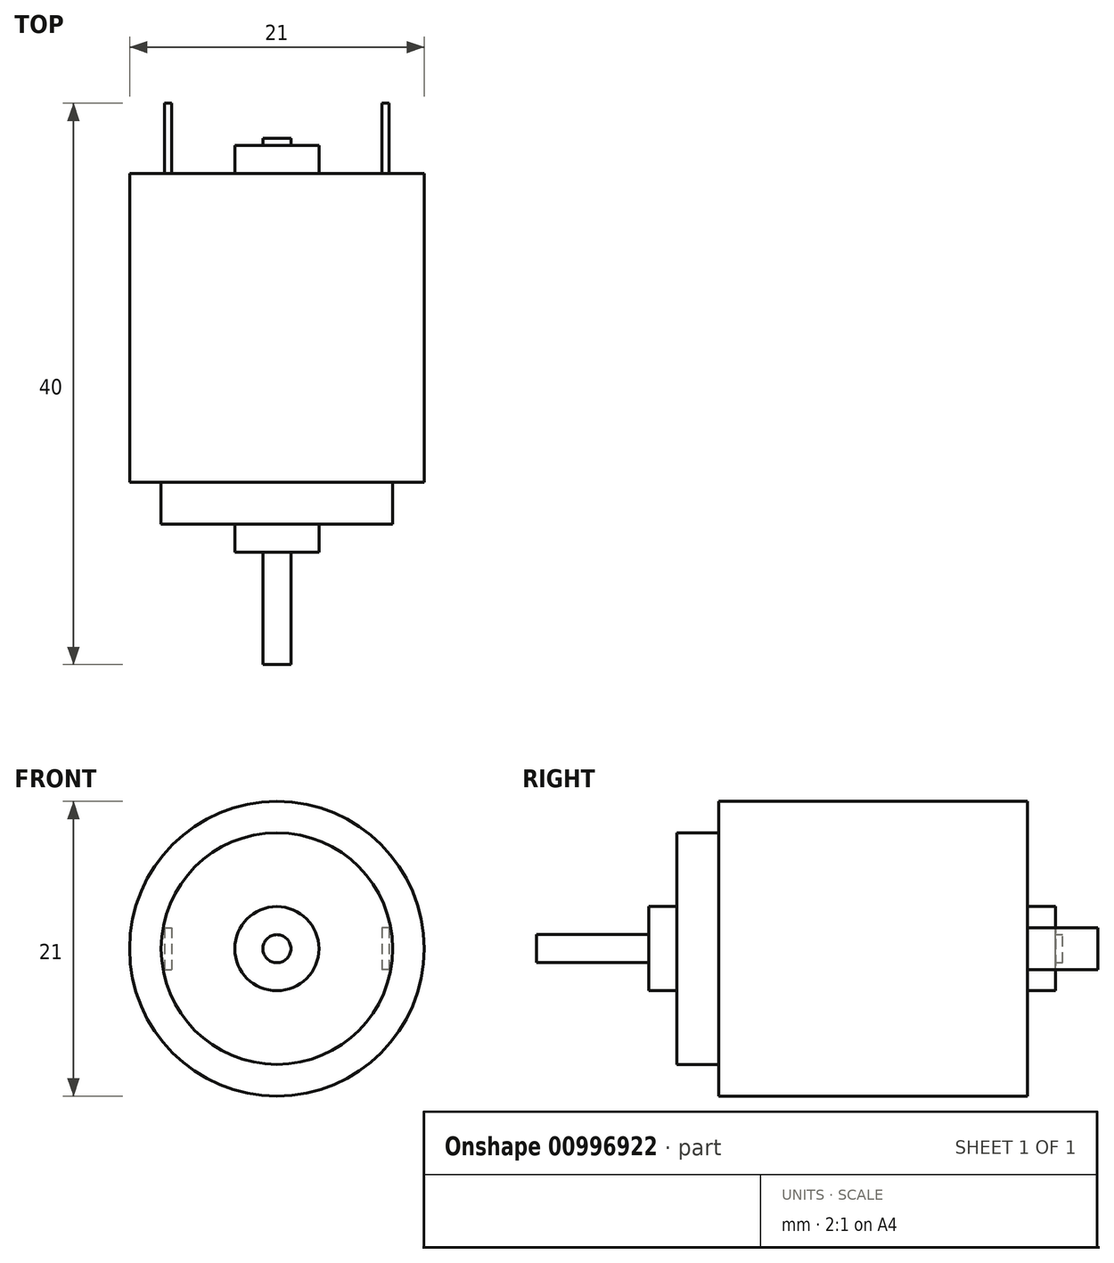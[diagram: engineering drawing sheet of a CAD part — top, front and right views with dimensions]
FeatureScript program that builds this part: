
annotation { "Feature Type Name" : "Feature", "Feature Type Description" : "" }
export const myFeature = defineFeature(function(context is Context, id is Id, definition is map)
    precondition{}
    {
        {
            var Q0;
            Q0=qCreatedBy(makeId("Front.planeOp"),FACE);
            var sketch = newSketch(context, id + "F0", { "sketchPlane" : qUnion([Q0])});
            skCircle(sketch, "E0", {"center": v(0, 0) * mm, "radius": 10.5 * mm});
            skCircle(sketch, "E1", {"center": v(0, 0) * mm, "radius": 8.25 * mm});
            skCircle(sketch, "E2", {"center": v(0, 0) * mm, "radius": 3 * mm});
            skCircle(sketch, "E3", {"center": v(0, 0) * mm, "radius": 1 * mm});
            skLineSegment(sketch, "E4", {"start": v(-10.5, 0) * mm, "end": v(-8, 0) * mm, "construction": true});
            skLineSegment(sketch, "E5", {"start": v(-8, 0) * mm, "end": v(-8, 1.5) * mm, "construction": true});
            skLineSegment(sketch, "E6.bottom", {"start": v(-8, 1.5) * mm, "end": v(-7.5, 1.5) * mm});
            skLineSegment(sketch, "E6.top", {"start": v(-8, -1.5) * mm, "end": v(-7.5, -1.5) * mm});
            skLineSegment(sketch, "E6.left", {"start": v(-8, 1.5) * mm, "end": v(-8, -1.5) * mm});
            skLineSegment(sketch, "E6.right", {"start": v(-7.5, 1.5) * mm, "end": v(-7.5, -1.5) * mm});
            skLineSegment(sketch, "E7.MirrorCS", {"start": v(7.5, 1.5) * mm, "end": v(7.5, -1.5) * mm});
            skLineSegment(sketch, "E8.MirrorCS", {"start": v(8, 1.5) * mm, "end": v(7.5, 1.5) * mm});
            skLineSegment(sketch, "E9.MirrorCS", {"start": v(8, 0) * mm, "end": v(8, 1.5) * mm, "construction": true});
            skLineSegment(sketch, "E10.MirrorCS", {"start": v(8, 1.5) * mm, "end": v(8, -1.5) * mm});
            skLineSegment(sketch, "E11.MirrorCS", {"start": v(8, -1.5) * mm, "end": v(7.5, -1.5) * mm});
            skSolve(sketch);
        }
        {
            var Q0;
            Q0=makeQuery(id+"F0.imprint","IMPRINT",FACE,{"disambiguationData":[TD([[makeQuery(id+"F0.imprint","IMPRINT",EDGE,{"derivedFrom":sQuery(id+"F0.wireOp",EDGE,"E0")}),1.0]])]});
            extrude(context, id + "F1", {"entities" : qUnion([Q0]), "depth" : 22 * mm, "offsetDistance" : 25 * mm});
        }
        {
            var Q0;
            Q0=makeQuery(id+"F0.imprint","IMPRINT",FACE,{"disambiguationData":[TD([[makeQuery(id+"F0.imprint","IMPRINT",EDGE,{"derivedFrom":sQuery(id+"F0.wireOp",EDGE,"E1")}),1.0]])]});
            var Q1;
            Q1=makeQuery(id+"F0.imprint","IMPRINT",FACE,{"disambiguationData":[TD([[makeQuery(id+"F0.imprint","IMPRINT",EDGE,{"derivedFrom":sQuery(id+"F0.wireOp",EDGE,"E6.bottom")}),-1.0]])]});
            var Q2;
            Q2=makeQuery(id+"F0.imprint","IMPRINT",FACE,{"disambiguationData":[TD([[makeQuery(id+"F0.imprint","IMPRINT",EDGE,{"derivedFrom":sQuery(id+"F0.wireOp",EDGE,"E7.MirrorCS")}),1.0]])]});
            extrude(context, id + "F2", {"entities" : qUnion([Q0, Q1, Q2]), "operationType" : NewBodyOperationType.ADD, "depth" : 25 * mm, "offsetDistance" : 25 * mm});
        }
        {
            var Q0;
            Q0=makeQuery(id+"F0.imprint","IMPRINT",FACE,{"disambiguationData":[TD([[makeQuery(id+"F0.imprint","IMPRINT",EDGE,{"derivedFrom":sQuery(id+"F0.wireOp",EDGE,"E2")}),1.0]])]});
            extrude(context, id + "F3", {"entities" : qUnion([Q0]), "operationType" : NewBodyOperationType.ADD, "depth" : 27 * mm, "offsetDistance" : 25 * mm, "hasSecondDirection" : true, "secondDirectionOppositeDirection" : true, "secondDirectionDepth" : 2 * mm});
        }
        {
            var Q0;
            Q0=makeQuery(id+"F0.imprint","IMPRINT",FACE,{"disambiguationData":[TD([[makeQuery(id+"F0.imprint","IMPRINT",EDGE,{"derivedFrom":sQuery(id+"F0.wireOp",EDGE,"E3")}),1.0]])]});
            var Q1;
            Q1=sQuery(id+"F0.wireOp",EDGE,"E3");
            extrude(context, id + "F4", {"entities" : qUnion([Q0]), "operationType" : NewBodyOperationType.ADD, "surfaceEntities" : qUnion([Q1]), "depth" : 35 * mm, "offsetDistance" : 25 * mm, "hasSecondDirection" : true, "secondDirectionOppositeDirection" : true, "secondDirectionDepth" : 2.5 * mm});
        }
        {
            var Q0;
            Q0=makeQuery(id+"F0.imprint","IMPRINT",FACE,{"disambiguationData":[TD([[makeQuery(id+"F0.imprint","IMPRINT",EDGE,{"derivedFrom":sQuery(id+"F0.wireOp",EDGE,"E6.bottom")}),-1.0]])]});
            var Q1;
            Q1=makeQuery(id+"F0.imprint","IMPRINT",FACE,{"disambiguationData":[TD([[makeQuery(id+"F0.imprint","IMPRINT",EDGE,{"derivedFrom":sQuery(id+"F0.wireOp",EDGE,"E7.MirrorCS")}),1.0]])]});
            extrude(context, id + "F5", {"entities" : qUnion([Q0, Q1]), "operationType" : NewBodyOperationType.ADD, "oppositeDirection" : true, "depth" : 5 * mm, "offsetDistance" : 25 * mm});
        }
    });
